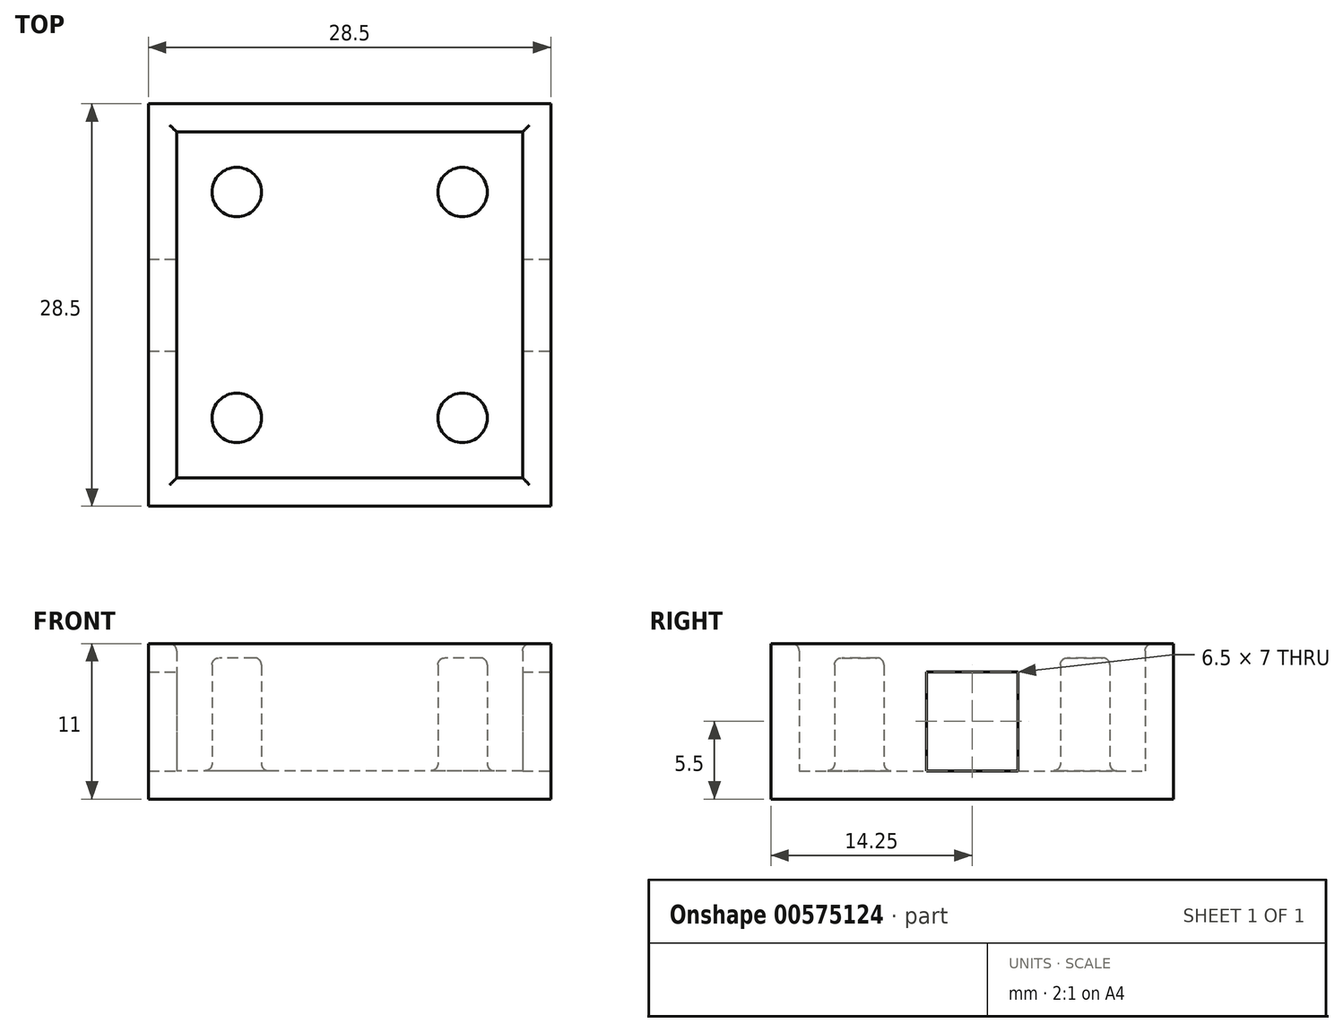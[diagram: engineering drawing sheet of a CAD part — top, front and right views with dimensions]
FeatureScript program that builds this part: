
annotation { "Feature Type Name" : "Feature", "Feature Type Description" : "" }
export const myFeature = defineFeature(function(context is Context, id is Id, definition is map)
    precondition{}
    {
        {
            var Q0;
            Q0=qCreatedBy(makeId("Top.planeOp"),FACE);
            var sketch = newSketch(context, id + "F0", { "sketchPlane" : qUnion([Q0])});
            skLineSegment(sketch, "E0.bottom", {"start": v(12.25, -12.25) * mm, "end": v(-12.25, -12.25) * mm});
            skLineSegment(sketch, "E0.top", {"start": v(12.25, 12.25) * mm, "end": v(-12.25, 12.25) * mm});
            skLineSegment(sketch, "E0.left", {"start": v(12.25, -12.25) * mm, "end": v(12.25, 12.25) * mm});
            skLineSegment(sketch, "E0.right", {"start": v(-12.25, -12.25) * mm, "end": v(-12.25, 12.25) * mm});
            skPoint(sketch, "E0.middle", {"position": v(0, 0) * mm});
            skSolve(sketch);
        }
        {
            var Q0;
            Q0 = qSketchRegion(id + "F0", true);
            extrude(context, id + "F1", {"entities" : qUnion([Q0]), "depth" : 1 * mm, "offsetDistance" : 25 * mm});
        }
        {
            var Q0;
            Q0=qCreatedBy(makeId("Top.planeOp"),FACE);
            var sketch = newSketch(context, id + "F2", { "sketchPlane" : qUnion([Q0])});
            skLineSegment(sketch, "E1.bottom", {"start": v(14.25, -14.25) * mm, "end": v(-14.25, -14.25) * mm});
            skLineSegment(sketch, "E1.top", {"start": v(14.25, 14.25) * mm, "end": v(-14.25, 14.25) * mm});
            skLineSegment(sketch, "E1.left", {"start": v(14.25, -14.25) * mm, "end": v(14.25, 14.25) * mm});
            skLineSegment(sketch, "E1.right", {"start": v(-14.25, -14.25) * mm, "end": v(-14.25, 14.25) * mm});
            skPoint(sketch, "E1.middle", {"position": v(0, 0) * mm});
            skLineSegment(sketch, "E2.bottom", {"start": v(12.25, -12.25) * mm, "end": v(-12.25, -12.25) * mm});
            skLineSegment(sketch, "E2.top", {"start": v(12.25, 12.25) * mm, "end": v(-12.25, 12.25) * mm});
            skLineSegment(sketch, "E2.left", {"start": v(12.25, -12.25) * mm, "end": v(12.25, 12.25) * mm});
            skLineSegment(sketch, "E2.right", {"start": v(-12.25, -12.25) * mm, "end": v(-12.25, 12.25) * mm});
            skSolve(sketch);
        }
        {
            var Q0;
            Q0 = qSketchRegion(id + "F2", true);
            extrude(context, id + "F3", {"entities" : qUnion([Q0]), "operationType" : NewBodyOperationType.ADD, "depth" : 10 * mm, "offsetDistance" : 25 * mm});
        }
        {
            var Q0;
            Q0=qCreatedBy(makeId("Right.planeOp"),FACE);
            var sketch = newSketch(context, id + "F4", { "sketchPlane" : qUnion([Q0])});
            skLineSegment(sketch, "E3.bottom", {"start": v(3.25, 1) * mm, "end": v(-3.25, 1) * mm});
            skLineSegment(sketch, "E3.top", {"start": v(3.25, 8) * mm, "end": v(-3.25, 8) * mm});
            skLineSegment(sketch, "E3.left", {"start": v(3.25, 1) * mm, "end": v(3.25, 8) * mm});
            skLineSegment(sketch, "E3.right", {"start": v(-3.25, 1) * mm, "end": v(-3.25, 8) * mm});
            skPoint(sketch, "E3.middle", {"position": v(0, 4.5) * mm});
            skSolve(sketch);
        }
        {
            var Q0;
            Q0 = qSketchRegion(id + "F4", true);
            extrude(context, id + "F5", {"entities" : qUnion([Q0]), "operationType" : NewBodyOperationType.REMOVE, "endBound" : BoundingType.SYMMETRIC, "oppositeDirection" : true, "depth" : 28.5 * mm, "offsetDistance" : 25 * mm});
        }
        {
            var Q0;
            Q0=qCreatedBy(makeId("Top.planeOp"),FACE);
            var sketch = newSketch(context, id + "F6", { "sketchPlane" : qUnion([Q0])});
            skCircle(sketch, "E4", {"center": v(-8, -8) * mm, "radius": 1.75 * mm});
            skCircle(sketch, "E5.MirrorC", {"center": v(8, -8) * mm, "radius": 1.75 * mm});
            skCircle(sketch, "E6.MirrorC", {"center": v(-8, 8) * mm, "radius": 1.75 * mm});
            skCircle(sketch, "E7.MirrorC", {"center": v(8, 8) * mm, "radius": 1.75 * mm});
            skSolve(sketch);
        }
        {
            var Q0;
            Q0 = qSketchRegion(id + "F6", true);
            extrude(context, id + "F7", {"entities" : qUnion([Q0]), "operationType" : NewBodyOperationType.ADD, "depth" : 9 * mm, "offsetDistance" : 25 * mm});
        }
        {
            var Q0;
            Q0 = qSketchRegion(id + "F0", true);
            extrude(context, id + "F8", {"entities" : qUnion([Q0]), "operationType" : NewBodyOperationType.ADD, "oppositeDirection" : true, "depth" : 1 * mm, "offsetDistance" : 25 * mm});
        }
        {
            var Q0;
            Q0 = qSketchRegion(id + "F2", true);
            extrude(context, id + "F9", {"entities" : qUnion([Q0]), "operationType" : NewBodyOperationType.ADD, "oppositeDirection" : true, "depth" : 1 * mm, "offsetDistance" : 25 * mm});
        }
        {
            var Q0;
            Q0=makeQuery(id+"F3.opExtrude","CAP_EDGE",EDGE,{"disambiguationData":[OSD([sQuery(id+"F2.wireOp",EDGE,"E2.bottom")])],"isStart":false});
            var Q1;
            Q1=makeQuery(id+"F3.opExtrude","CAP_EDGE",EDGE,{"disambiguationData":[OSD([sQuery(id+"F2.wireOp",EDGE,"E2.left")])],"isStart":false});
            var Q2;
            Q2=makeQuery(id+"F3.opExtrude","CAP_EDGE",EDGE,{"disambiguationData":[OSD([sQuery(id+"F2.wireOp",EDGE,"E2.top")])],"isStart":false});
            var Q3;
            Q3=makeQuery(id+"F3.opExtrude","CAP_EDGE",EDGE,{"disambiguationData":[OSD([sQuery(id+"F2.wireOp",EDGE,"E2.right")])],"isStart":false});
            var Q4;
            Q4=makeQuery(id+"F7.opExtrude","CAP_EDGE",EDGE,{"disambiguationData":[OSD([sQuery(id+"F6.wireOp",EDGE,"E4")])],"isStart":false});
            var Q5;
            Q5=makeQuery(id+"F7.opExtrude","CAP_EDGE",EDGE,{"disambiguationData":[OSD([sQuery(id+"F6.wireOp",EDGE,"E6.MirrorC")])],"isStart":false});
            var Q6;
            Q6=makeQuery(id+"F7.opExtrude","CAP_EDGE",EDGE,{"disambiguationData":[OSD([sQuery(id+"F6.wireOp",EDGE,"E7.MirrorC")])],"isStart":false});
            var Q7;
            Q7=makeQuery(id+"F7.opExtrude","CAP_EDGE",EDGE,{"disambiguationData":[OSD([sQuery(id+"F6.wireOp",EDGE,"E5.MirrorC")])],"isStart":false});
            var Q8;
            Q8=makeQuery(id+"F7.boolean.opBoolean","INTERSECT",EDGE,{"derivedFrom":[makeQuery(id+"F5.boolean.opBoolean","MERGE",FACE,{"derivedFrom":[makeQuery(id+"F1.opExtrude","CAP_FACE",FACE,{"disambiguationData":[OSD([sQuery(id+"F0.wireOp",EDGE,"E0.bottom"),sQuery(id+"F0.wireOp",EDGE,"E0.top"),sQuery(id+"F0.wireOp",EDGE,"E0.left"),sQuery(id+"F0.wireOp",EDGE,"E0.right")])],"isStart":false}),makeQuery(id+"F5.opExtrude","SWEPT_FACE",FACE,{"disambiguationData":[OSD([sQuery(id+"F4.wireOp",EDGE,"E3.bottom")])]})]}),makeQuery(id+"F7.opExtrude","SWEPT_FACE",FACE,{"disambiguationData":[OSD([sQuery(id+"F6.wireOp",EDGE,"E6.MirrorC")])]})]});
            var Q9;
            Q9=makeQuery(id+"F7.boolean.opBoolean","INTERSECT",EDGE,{"derivedFrom":[makeQuery(id+"F5.boolean.opBoolean","MERGE",FACE,{"derivedFrom":[makeQuery(id+"F1.opExtrude","CAP_FACE",FACE,{"disambiguationData":[OSD([sQuery(id+"F0.wireOp",EDGE,"E0.bottom"),sQuery(id+"F0.wireOp",EDGE,"E0.top"),sQuery(id+"F0.wireOp",EDGE,"E0.left"),sQuery(id+"F0.wireOp",EDGE,"E0.right")])],"isStart":false}),makeQuery(id+"F5.opExtrude","SWEPT_FACE",FACE,{"disambiguationData":[OSD([sQuery(id+"F4.wireOp",EDGE,"E3.bottom")])]})]}),makeQuery(id+"F7.opExtrude","SWEPT_FACE",FACE,{"disambiguationData":[OSD([sQuery(id+"F6.wireOp",EDGE,"E4")])]})]});
            var Q10;
            Q10=makeQuery(id+"F7.boolean.opBoolean","INTERSECT",EDGE,{"derivedFrom":[makeQuery(id+"F5.boolean.opBoolean","MERGE",FACE,{"derivedFrom":[makeQuery(id+"F1.opExtrude","CAP_FACE",FACE,{"disambiguationData":[OSD([sQuery(id+"F0.wireOp",EDGE,"E0.bottom"),sQuery(id+"F0.wireOp",EDGE,"E0.top"),sQuery(id+"F0.wireOp",EDGE,"E0.left"),sQuery(id+"F0.wireOp",EDGE,"E0.right")])],"isStart":false}),makeQuery(id+"F5.opExtrude","SWEPT_FACE",FACE,{"disambiguationData":[OSD([sQuery(id+"F4.wireOp",EDGE,"E3.bottom")])]})]}),makeQuery(id+"F7.opExtrude","SWEPT_FACE",FACE,{"disambiguationData":[OSD([sQuery(id+"F6.wireOp",EDGE,"E5.MirrorC")])]})]});
            var Q11;
            Q11=makeQuery(id+"F7.boolean.opBoolean","INTERSECT",EDGE,{"derivedFrom":[makeQuery(id+"F5.boolean.opBoolean","MERGE",FACE,{"derivedFrom":[makeQuery(id+"F1.opExtrude","CAP_FACE",FACE,{"disambiguationData":[OSD([sQuery(id+"F0.wireOp",EDGE,"E0.bottom"),sQuery(id+"F0.wireOp",EDGE,"E0.top"),sQuery(id+"F0.wireOp",EDGE,"E0.left"),sQuery(id+"F0.wireOp",EDGE,"E0.right")])],"isStart":false}),makeQuery(id+"F5.opExtrude","SWEPT_FACE",FACE,{"disambiguationData":[OSD([sQuery(id+"F4.wireOp",EDGE,"E3.bottom")])]})]}),makeQuery(id+"F7.opExtrude","SWEPT_FACE",FACE,{"disambiguationData":[OSD([sQuery(id+"F6.wireOp",EDGE,"E7.MirrorC")])]})]});
            fillet(context, id + "F10", {"entities" : qUnion([Q0, Q1, Q2, Q3, Q4, Q5, Q6, Q7, Q8, Q9, Q10, Q11]), "radius" : 0.5 * mm, "tangentPropagation" : true, "allowEdgeOverflow" : false});
        }
    });
